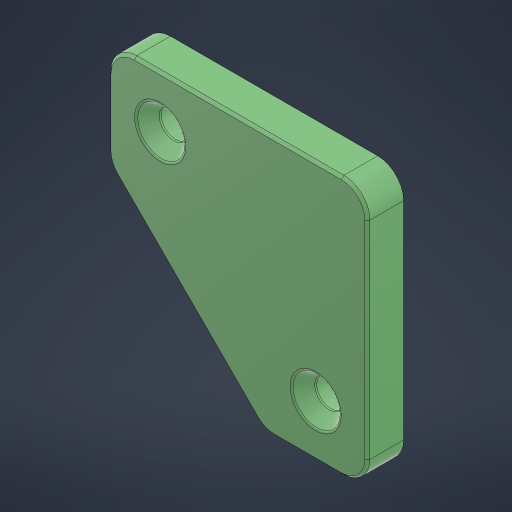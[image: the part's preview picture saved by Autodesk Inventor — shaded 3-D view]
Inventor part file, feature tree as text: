
AUTODESK INVENTOR PART (.ipt)
format: ipt  version: 2024 (Build 280153000, 153)  size: 308,224 bytes
history: native  units: mm
features: other x7, extrude x5, sketch x5, chamfer x4, fillet x4
ambient origin geometry x8: Origin, YZ Plane, XZ Plane, XY Plane, X Axis, Y Axis, Z Axis, Center Point
bodies: Body1 (feature_tree)
feature tree (25):
  other  "솔리드1"
  extrude  "돌출1"  Depth=50.0mm
  extrude  "돌출2"  Depth=50.0mm
  chamfer  "모따기2"  Distance=20.0mm
  fillet  "모깎기3"  Radius=20.0mm
  chamfer  "모따기3"  Distance=7.0mm
  fillet  "모깎기4"  Radius=10.0mm
  extrude  "돌출3"  Depth=10.0mm
  extrude  "돌출4"  Depth=10.0mm
  chamfer  "모따기4"  Distance=10.0mm
  fillet  "모깎기5"  Radius=5.4mm
  fillet  "모깎기6"  Radius=5.4mm
  chamfer  "모따기5"  Distance=10.0mm
  extrude  "돌출5"  Depth=2.0mm
  sketch  "스케치1"
  sketch  "스케치2"
  sketch  "스케치3"
  sketch  "스케치4"
  sketch  "스케치6"
  other  "Finish1"
  other  "Finish2"
  other  "Finish3"
  other  "Finish4"
  other  "Finish5"
  other  "Finish6"
